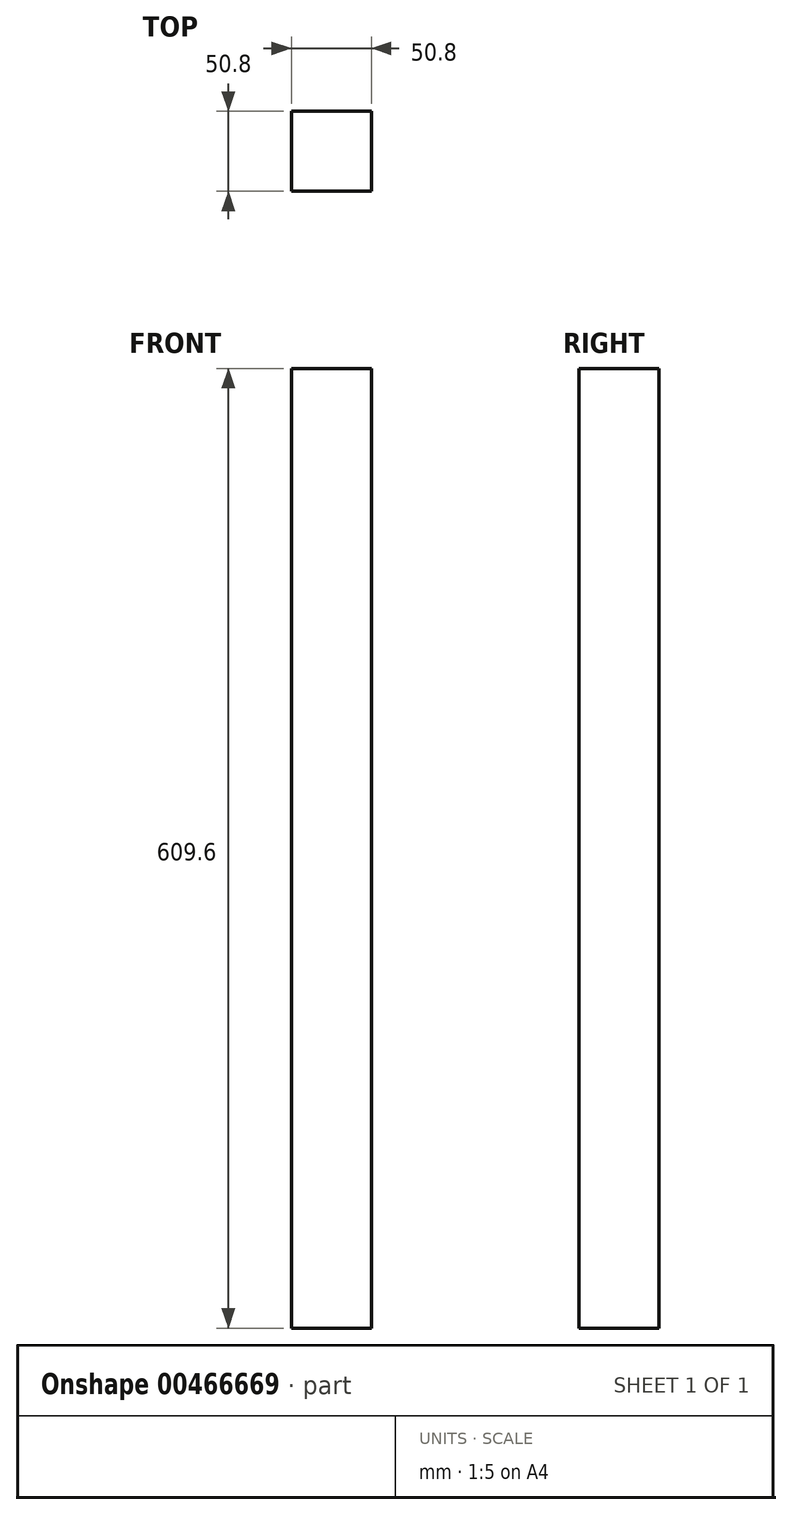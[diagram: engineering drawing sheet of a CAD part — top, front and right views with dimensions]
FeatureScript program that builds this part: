
annotation { "Feature Type Name" : "Feature", "Feature Type Description" : "" }
export const myFeature = defineFeature(function(context is Context, id is Id, definition is map)
    precondition{}
    {
        {
            var Q0;
            Q0=qCreatedBy(makeId("Top.planeOp"),FACE);
            var sketch = newSketch(context, id + "F0", { "sketchPlane" : qUnion([Q0])});
            skLineSegment(sketch, "E0.bottom", {"start": v(-25.4, 25.4) * mm, "end": v(25.4, 25.4) * mm});
            skLineSegment(sketch, "E0.top", {"start": v(-25.4, -25.4) * mm, "end": v(25.4, -25.4) * mm});
            skLineSegment(sketch, "E0.left", {"start": v(-25.4, 25.4) * mm, "end": v(-25.4, -25.4) * mm});
            skLineSegment(sketch, "E0.right", {"start": v(25.4, 25.4) * mm, "end": v(25.4, -25.4) * mm});
            skPoint(sketch, "E0.middle", {"position": v(0, 0) * mm});
            skSolve(sketch);
        }
        {
            var Q0;
            Q0=makeQuery(id+"F0.imprint","IMPRINT",FACE,{"disambiguationData":[TD([[makeQuery(id+"F0.imprint","IMPRINT",EDGE,{"derivedFrom":sQuery(id+"F0.wireOp",EDGE,"E0.bottom")}),-1.0]])]});
            extrude(context, id + "F1", {"entities" : qUnion([Q0]), "depth" : 609.6 * mm});
        }
    });
